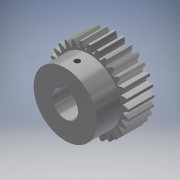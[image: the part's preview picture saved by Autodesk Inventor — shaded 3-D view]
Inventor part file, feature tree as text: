
AUTODESK INVENTOR PART (.ipt)
format: ipt  version: 2019 (Build 230136000, 136)  size: 306,688 bytes
history: native  units: mm (DEFAULTED — no unit token found)
features: sketch x5, plane x4, extrude x3, other x3, hole x1, projected_geometry x1
ambient origin geometry x8: Origin, YZ Plane, XZ Plane, XY Plane, X Axis, Y Axis, Z Axis, Center Point
bodies: Solid1 (feature_tree)
feature tree (17):
  extrude  "Extrusion1"  Depth=15.0mm TaperAngle=0.0deg
  plane  "Work Plane2"
  plane  "Work Plane8"
  plane  "Work Plane9"
  other  "正齒輪"
  extrude  "擠出2"  Depth=10.0mm TaperAngle=0.0deg
  extrude  "擠出3"  Depth=29.0mm
  plane  "工作平面11"
  hole  "孔1"  [1 undecoded]
  sketch  "Sketch1"  dims[d0=46.466966mm d1=15.0mm d2=0.0mm]
  sketch  "Sketch2"  dims[d3=43.889556mm d4=10.0mm d5=0.0mm d16=56.753736mm d17=0.0mm d34=1.083308mm d39=0.0mm d41=0.0mm d43=56.753736mm d46=56.753736mm d47=0.0mm d48=0.0mm d49=15.0mm d50=29.0mm d51=0.0mm d52=37.0mm d53=2.0mm d54=5.0mm d55=2.0mm d56=14.0mm d57=0.0mm d58=3.242mm d59=8.0mm d60=4.0mm d61=2.0mm d62=90.0deg d63=8.0mm d64=20.594885mm d65=5.833761mm]
  other  "Srf1"
  sketch  "草圖3"
  sketch  "草圖4"
  sketch  "草圖5"
  projected_geometry  "投影迴路1"
  other  "節圓直徑"
note: 1 required parameter value undecoded (feature->parameter linkage not recoverable at this tier; creation-order binding heuristic only, values carry confidence <= 0.55)
